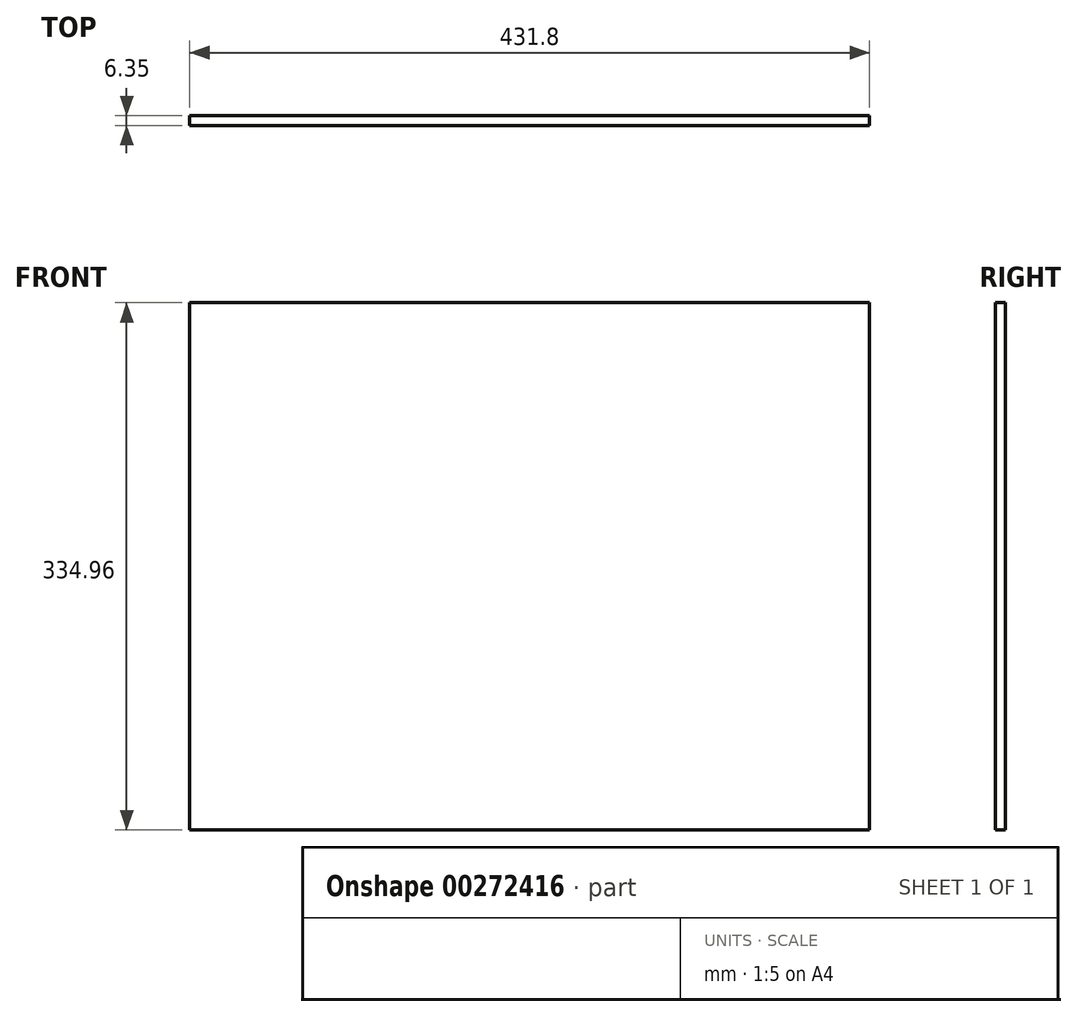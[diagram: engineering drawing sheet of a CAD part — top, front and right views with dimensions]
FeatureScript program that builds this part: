
annotation { "Feature Type Name" : "Feature", "Feature Type Description" : "" }
export const myFeature = defineFeature(function(context is Context, id is Id, definition is map)
    precondition{}
    {
        {
            var Q0;
            Q0=qCreatedBy(makeId("Front.planeOp"),FACE);
            var sketch = newSketch(context, id + "F0", { "sketchPlane" : qUnion([Q0])});
            skLineSegment(sketch, "E0.bottom", {"start": v(-204.96, 227.88) * mm, "end": v(226.84, 227.88) * mm});
            skLineSegment(sketch, "E0.top", {"start": v(-204.96, -107.08) * mm, "end": v(226.84, -107.08) * mm});
            skLineSegment(sketch, "E0.left", {"start": v(-204.96, 227.88) * mm, "end": v(-204.96, -107.08) * mm});
            skLineSegment(sketch, "E0.right", {"start": v(226.84, 227.88) * mm, "end": v(226.84, -107.08) * mm});
            skSolve(sketch);
        }
        {
            var Q0;
            Q0=makeQuery(id+"F0.imprint","IMPRINT",FACE,{"disambiguationData":[TD([[makeQuery(id+"F0.imprint","IMPRINT",EDGE,{"derivedFrom":sQuery(id+"F0.wireOp",EDGE,"E0.bottom")}),-1.0]])]});
            extrude(context, id + "F1", {"entities" : qUnion([Q0]), "depth" : 6.35 * mm});
        }
    });
